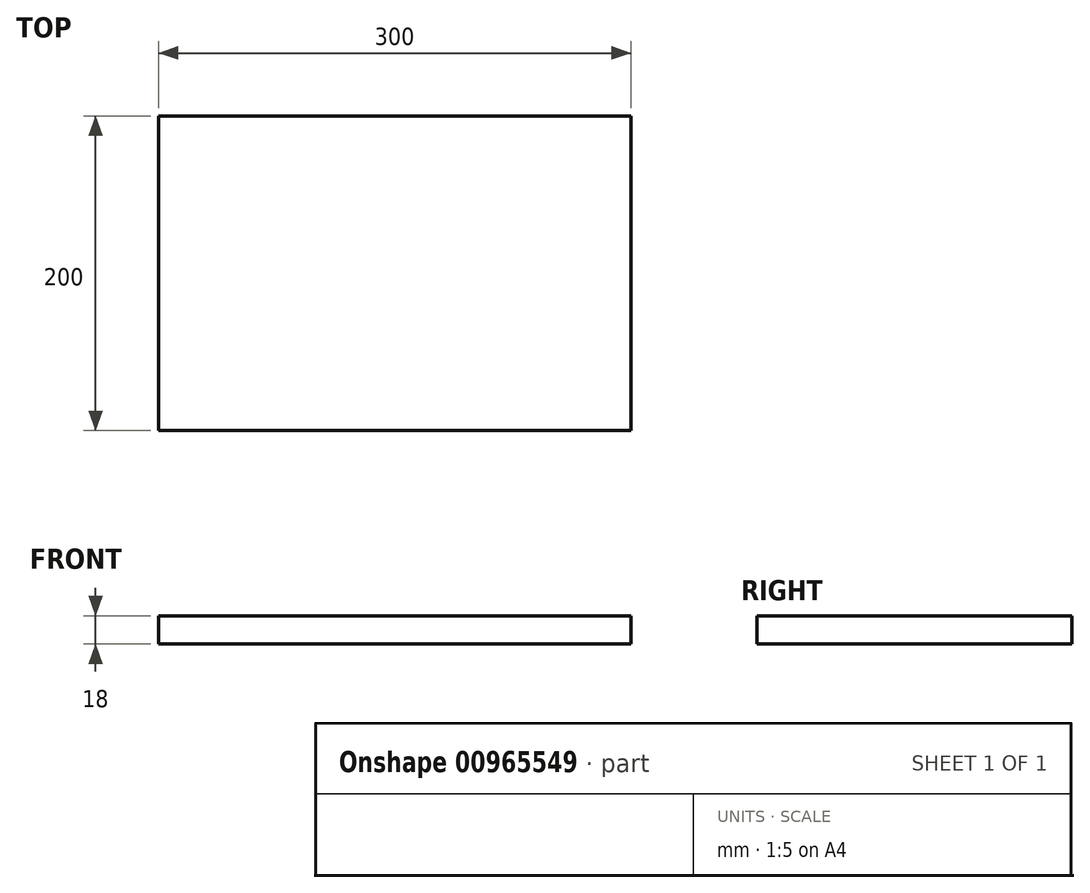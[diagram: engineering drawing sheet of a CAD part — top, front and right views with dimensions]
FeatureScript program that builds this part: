
annotation { "Feature Type Name" : "Feature", "Feature Type Description" : "" }
export const myFeature = defineFeature(function(context is Context, id is Id, definition is map)
    precondition{}
    {
        {
            var Q0;
            Q0=qCreatedBy(makeId("Top.planeOp"),FACE);
            var sketch = newSketch(context, id + "F0", { "sketchPlane" : qUnion([Q0])});
            skLineSegment(sketch, "E0.bottom", {"start": v(150, 100) * mm, "end": v(-150, 100) * mm});
            skLineSegment(sketch, "E0.top", {"start": v(150, -100) * mm, "end": v(-150, -100) * mm});
            skLineSegment(sketch, "E0.left", {"start": v(150, 100) * mm, "end": v(150, -100) * mm});
            skLineSegment(sketch, "E0.right", {"start": v(-150, 100) * mm, "end": v(-150, -100) * mm});
            skPoint(sketch, "E0.middle", {"position": v(0, 0) * mm});
            skSolve(sketch);
        }
        {
            var Q0;
            Q0=makeQuery(id+"F0.imprint","IMPRINT",FACE,{"disambiguationData":[TD([[makeQuery(id+"F0.imprint","IMPRINT",EDGE,{"derivedFrom":sQuery(id+"F0.wireOp",EDGE,"E0.bottom")}),1.0]])]});
            extrude(context, id + "F1", {"entities" : qUnion([Q0]), "depth" : 18 * mm, "offsetDistance" : 25 * mm});
        }
    });
